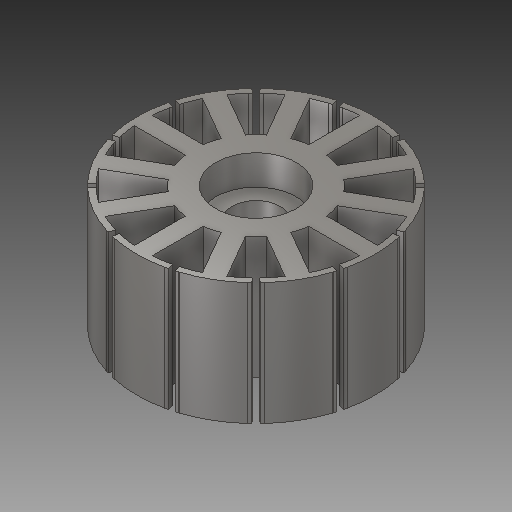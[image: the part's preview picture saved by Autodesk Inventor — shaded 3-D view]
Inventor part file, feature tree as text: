
AUTODESK INVENTOR PART (.ipt)
format: ipt  version: 2019.3 (Build 233278000, 278)  size: 309,760 bytes
history: native  units: mm
features: plane x1
ambient origin geometry x8: Origin, YZ Plane, XZ Plane, XY Plane, X Axis, Y Axis, Z Axis, Center Point
bodies: Solid1 (feature_tree), Body1 (feature_tree)
feature tree (1):
  plane  "Work Plane1"
